# Revit family: Toilet-Dual_Flush-Right_Height-Elongated-American_Standard-H2Option-2886_Series
name_source: partatom
category: Plumbing Fixtures
units: mm (PartAtom-declared; Revit-internal decimal feet)

## family parameters
Always vertical = No
Cut with Voids When Loaded = No
OmniClass Number = 23.45.05.21.11.11
OmniClass Title = Water Operated Water Closets
Part Type = Normal
Room Calculation Point = No
Round Connector Dimension = Use Radius
Shared = Yes
Work Plane-Based = Yes

## types (2) — shared parameters
ADA Compliant = Yes
Assembly Code = D2010110
Bowl Shape = Elongated
CW Connection = Yes
CWFU = 5
Cold Water Connection Diameter = 3/8"
Cold Water Connection Height = 10"
Cold Water Connection Radius = 3/16"
Cold Water Connection Width = 6"
Default Elevation = 0"
Flush Rate = 0.92gpf-1.28gpf (3.4Lpf-4.8Lpf)
HW Connection = No
Height = 31"
Installation Type = Floor Mounted
Length = 29 3/4"
Manufacturer = American Standard
Material = Vitreous China-American Standard-020-White
Price = Prices may vary. Please consult Manufacturer Representative for most up-to-date price list.
Product Documentation Link = https://www.americanstandard-us.com
Product Page URL = https://www.americanstandard-us.com
URL = http://www.americanstandard-us.com
Vent Connection = No
WFU = 5
Warranty Information = 5 Years Limited
Waste Connection = Yes
Waste Connection Diameter = 2 1/8"
Waste Connection Radius = 1 1/16"
Width = 15"
zero-valued in all types: HWFU

## per-type parameters (varying)
| type | Description | Left Hand Trip Lever | Right Hand Trip Lever |
| 2886.204 | H2Option® ADA Dual Flush Right Height® Elongated Toilet Vitreous China Gloss Acrylic Left Lever | Yes | No |
| 2886.205 | H2Option® ADA Dual Flush Right Height® Elongated Toilet Vitreous China Gloss Acrylic Right Lever | No | Yes |

note: column(s) folded — value = type name in every type: Model

## geometry (parser evidence)
native form markers: Sweep x2
no freeform markers — native parametric forms only
